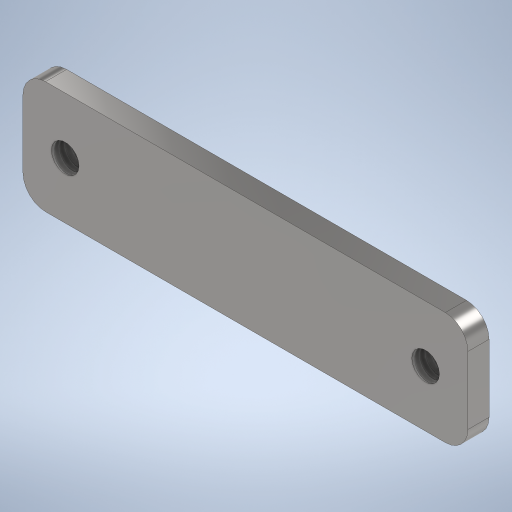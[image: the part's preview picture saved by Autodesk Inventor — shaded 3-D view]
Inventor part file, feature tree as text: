
AUTODESK INVENTOR PART (.ipt)
format: ipt  version: 2024 (Build 280153000, 153)  size: 233,984 bytes
history: native  units: in
note: dims shown in document units (in); Inventor stores cm internally (conversion verified against a paired STEP export)
features: sketch x1, extrude x1, fillet x1, hole x1
ambient origin geometry x8: Origin, YZ Plane, XZ Plane, XY Plane, X Axis, Y Axis, Z Axis, Center Point
bodies: Solid1 (feature_tree)
feature tree (4):
  sketch  "Sketch1"  dims[d0=1.5551in d1=0.3937in d3=0.074in d4=0.0in d5=0.0787in d6=1.2598in d7=0.0968in d8=0.2362in d9=0.2165in d10=0.0984in d11=90.0deg d12=0.3465in d13=0.0in]
  extrude  "Extrusion1"  Depth=0.3937in
  fillet  "Fillet1"  Radius=0.074in
  hole  "Hole1"  [1 undecoded]
note: 1 required parameter value undecoded (feature->parameter linkage not recoverable at this tier; creation-order binding heuristic only, values carry confidence <= 0.55)
